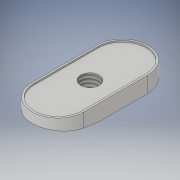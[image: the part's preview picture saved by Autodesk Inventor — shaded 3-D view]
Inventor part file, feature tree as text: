
AUTODESK INVENTOR PART (.ipt)
format: ipt  version: 2018 (Build 220112000, 112)  size: 150,528 bytes
history: native  units: in
note: dims shown in document units (in); Inventor stores cm internally (conversion verified against a paired STEP export)
features: sketch x6, extrude x4, hole x1, thread x1, plane x1, revolve x1
ambient origin geometry x8: Origin, YZ Plane, XZ Plane, XY Plane, X Axis, Y Axis, Z Axis, Center Point
bodies: Solid1 (feature_tree)
feature tree (14):
  extrude  "Extrusion1"  Depth=0.02in TaperAngle=0.0deg
  extrude  "Extrusion2"  Depth=0.25in TaperAngle=0.0deg
  hole  "Hole1"  [1 undecoded]
  thread  "Thread1"  [1 undecoded]
  extrude  "Extrusion3"  Depth=0.18in
  plane  "Work Plane1"
  revolve  "Revolution1"  [1 undecoded]
  extrude  "Extrusion4"  Depth=0.05in
  sketch  "Sketch1"  dims[d3=0.22in d4=0.0in d8=0.02in d9=0.0in]
  sketch  "Sketch2"  dims[d10=0.25in]
  sketch  "Sketch3"  dims[d11=0.25in d12=0.75in d13=0.375in d14=0.25in d15=0.5635in d16=1.0in d17=0.8108in d18=1.0in d19=0.0in]
  sketch  "Sketch4"  dims[d20=0.02in d21=0.0in d22=0.1in d23=0.5in]
  sketch  "Sketch5"  dims[d24=90.0deg d25=0.18in]
  sketch  "Sketch6"  dims[d26=0.4375in d27=0.05in d28=0.0in d29=0.0618in d30=0.24in d31=0.54in]
note: 3 required parameter values undecoded (feature->parameter linkage not recoverable at this tier; creation-order binding heuristic only, values carry confidence <= 0.55)